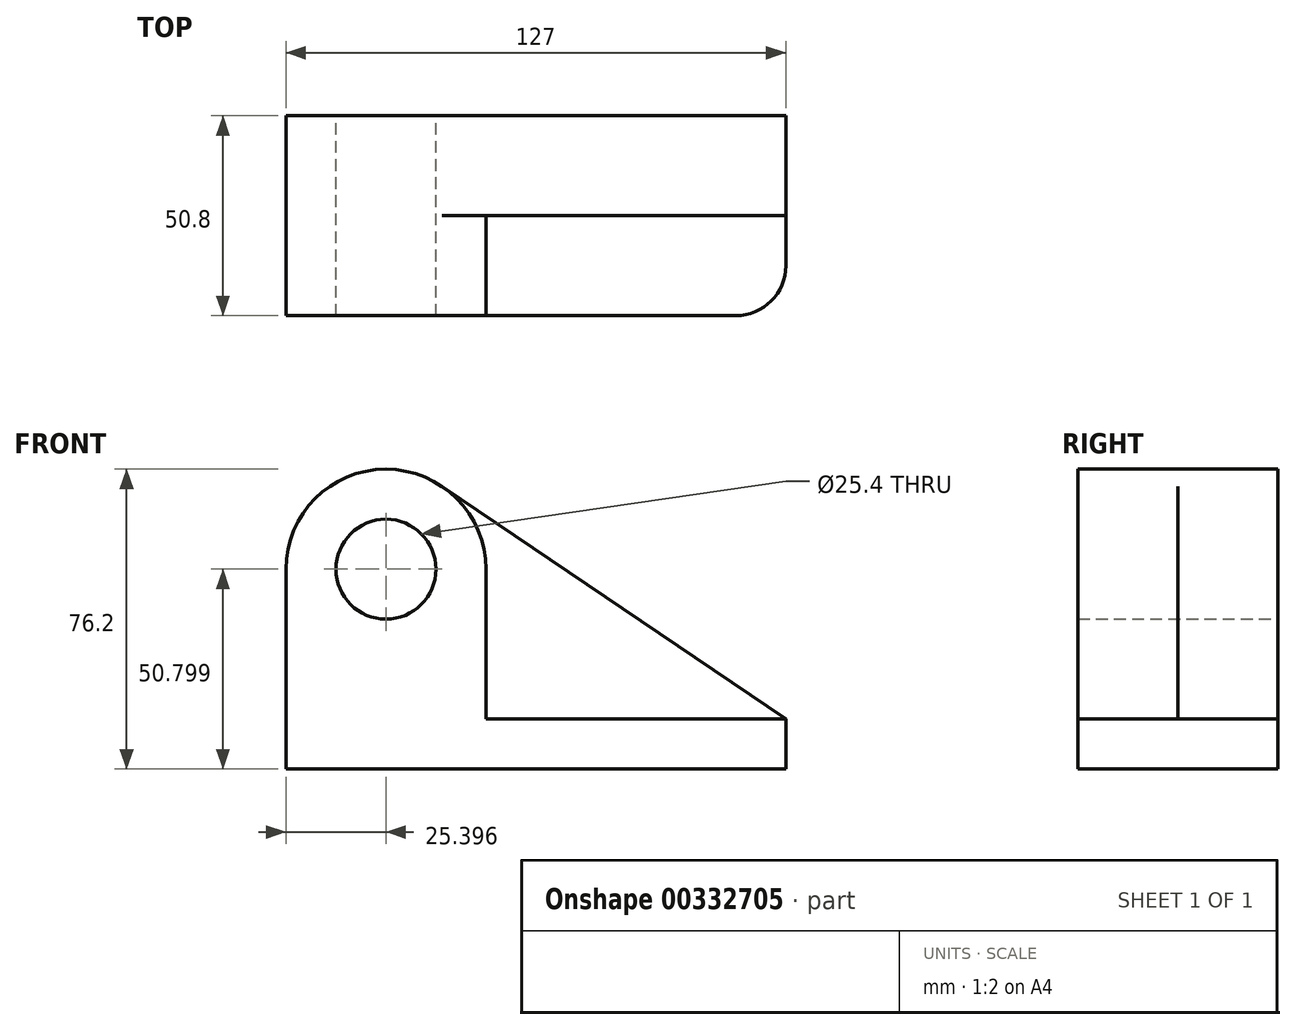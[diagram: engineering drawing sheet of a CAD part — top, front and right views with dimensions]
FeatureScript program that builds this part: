
annotation { "Feature Type Name" : "Feature", "Feature Type Description" : "" }
export const myFeature = defineFeature(function(context is Context, id is Id, definition is map)
    precondition{}
    {
        {
            var Q0;
            Q0=qCreatedBy(makeId("Front.planeOp"),FACE);
            var sketch = newSketch(context, id + "F0", { "sketchPlane" : qUnion([Q0])});
            skCircle(sketch, "E0", {"center": v(-87.75, 27.4) * mm, "radius": 12.7 * mm});
            skArc(sketch, "E1", {"start": v(-73.52, 48.43) * mm, "mid": v(-99.66, 49.84) * mm, "end": v(-113.15, 27.4) * mm});
            skLineSegment(sketch, "E2", {"start": v(-113.15, 27.4) * mm, "end": v(-113.15, -23.4) * mm});
            skLineSegment(sketch, "E3", {"start": v(-113.15, -23.4) * mm, "end": v(13.85, -23.4) * mm});
            skLineSegment(sketch, "E4", {"start": v(13.85, -23.4) * mm, "end": v(13.85, -10.7) * mm});
            skLineSegment(sketch, "E5", {"start": v(13.85, -10.7) * mm, "end": v(-73.52, 48.43) * mm});
            skSolve(sketch);
        }
        {
            var Q0;
            Q0=makeQuery(id+"F0.imprint","IMPRINT",FACE,{"disambiguationData":[TD([[makeQuery(id+"F0.imprint","IMPRINT",EDGE,{"derivedFrom":sQuery(id+"F0.wireOp",EDGE,"E0")}),-1.0]])]});
            extrude(context, id + "F1", {"entities" : qUnion([Q0]), "depth" : 25.4 * mm});
        }
        {
            var Q0;
            Q0=makeQuery(id+"F1.opExtrude","CAP_FACE",FACE,{"disambiguationData":[OSD([sQuery(id+"F0.wireOp",EDGE,"E0"),sQuery(id+"F0.wireOp",EDGE,"E1"),sQuery(id+"F0.wireOp",EDGE,"E2"),sQuery(id+"F0.wireOp",EDGE,"E3"),sQuery(id+"F0.wireOp",EDGE,"E4"),sQuery(id+"F0.wireOp",EDGE,"E5")])],"isStart":false});
            var sketch = newSketch(context, id + "F2", { "sketchPlane" : qUnion([Q0])});
            skCircle(sketch, "E6", {"center": v(-87.75, 27.4) * mm, "radius": 12.7 * mm});
            skArc(sketch, "E7", {"start": v(-62.35, 27.4) * mm, "mid": v(-87.75, 52.8) * mm, "end": v(-113.15, 27.4) * mm});
            skLineSegment(sketch, "E8.bottom", {"start": v(13.85, -10.7) * mm, "end": v(-62.35, -10.7) * mm});
            skLineSegment(sketch, "E8.top", {"start": v(13.85, -10.7) * mm, "end": v(-62.35, -10.7) * mm});
            skLineSegment(sketch, "E8.left", {"start": v(13.85, -10.7) * mm, "end": v(13.85, -10.7) * mm});
            skLineSegment(sketch, "E8.right", {"start": v(-113.15, -10.7) * mm, "end": v(-113.15, -10.7) * mm});
            skLineSegment(sketch, "E9", {"start": v(-62.35, 27.4) * mm, "end": v(-62.35, -10.7) * mm});
            skLineSegment(sketch, "E10", {"start": v(-113.15, 27.4) * mm, "end": v(-113.15, -10.7) * mm});
            skSolve(sketch);
        }
        {
            var Q0;
            Q0=makeQuery(id+"F2.imprint","IMPRINT",FACE,{"disambiguationData":[TD([[makeQuery(id+"F2.imprint","IMPRINT",EDGE,{"derivedFrom":sQuery(id+"F2.wireOp",EDGE,"E6")}),-1.0]])]});
            extrude(context, id + "F3", {"entities" : qUnion([Q0]), "operationType" : NewBodyOperationType.ADD, "depth" : 25.4 * mm});
        }
        {
            var Q0;
            Q0=makeQuery(id+"F3.opExtrude","CAP_EDGE",EDGE,{"disambiguationData":[OSD([sQuery(id+"F0.wireOp",EDGE,"E4")])],"isStart":false});
            fillet(context, id + "F4", {"entities" : qUnion([Q0]), "radius" : 12.7 * mm, "tangentPropagation" : true, "allowEdgeOverflow" : false});
        }
    });
